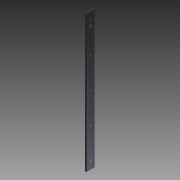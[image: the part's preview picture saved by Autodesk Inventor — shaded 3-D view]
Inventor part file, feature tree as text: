
AUTODESK INVENTOR PART (.ipt)
format: ipt  version: 2011 SP1 (Build 150282100, 282)  size: 130,560 bytes
history: native  units: mm
features: other x14, sketch x7, extrude x6, hole x1
ambient origin geometry x8: Origin, YZ Plane, XZ Plane, XY Plane, X Axis, Y Axis, Z Axis, Center Point
bodies: Solid1 (feature_tree)
feature tree (28):
  extrude  "Extrusion1"  Depth=1.0mm TaperAngle=0.0deg
  hole  "Hole1"  [1 undecoded]
  extrude  "Extrusion2"  Depth=1.0mm TaperAngle=0.0deg
  extrude  "Extrusion3"  [1 undecoded]
  extrude  "Extrusion4"  [1 undecoded]
  extrude  "Extrusion5"  [1 undecoded]
  extrude  "Extrusion6"  [1 undecoded]
  other  "to_body_XY"
  other  "to_body_YZ"
  other  "to_body_ZX"
  other  "to_body_X"
  other  "to_body_Y"
  other  "to_body_Z"
  other  "to_body_Center"
  other  "to_slider_XY"
  other  "to_slider_YZ"
  other  "to_slider_ZX"
  other  "to_slider_X"
  other  "to_slider_Y"
  other  "to_slider_Z"
  other  "to_slider_Center"
  sketch  "Sketch_1"  dims[d0=457.2mm d1=0.0mm]
  sketch  "Sketch2"  dims[d2=9.5mm d3=6.0mm d4=4.0mm d5=2.0mm d6=90.0deg d7=1.0mm d8=0.0mm d9=1.0mm d10=0.0mm]
  sketch  "Sketch_5"  dims[d11=1.0mm d12=0.0mm d13=1.0mm d14=0.0mm]
  sketch  "Sketch_6"  dims[d15=1.0mm d16=0.0mm d17=1.0mm d18=0.0mm]
  sketch  "Sketch_7"
  sketch  "Sketch_8"
  sketch  "Sketch_9"
note: 5 required parameter values undecoded (feature->parameter linkage not recoverable at this tier; creation-order binding heuristic only, values carry confidence <= 0.55)
